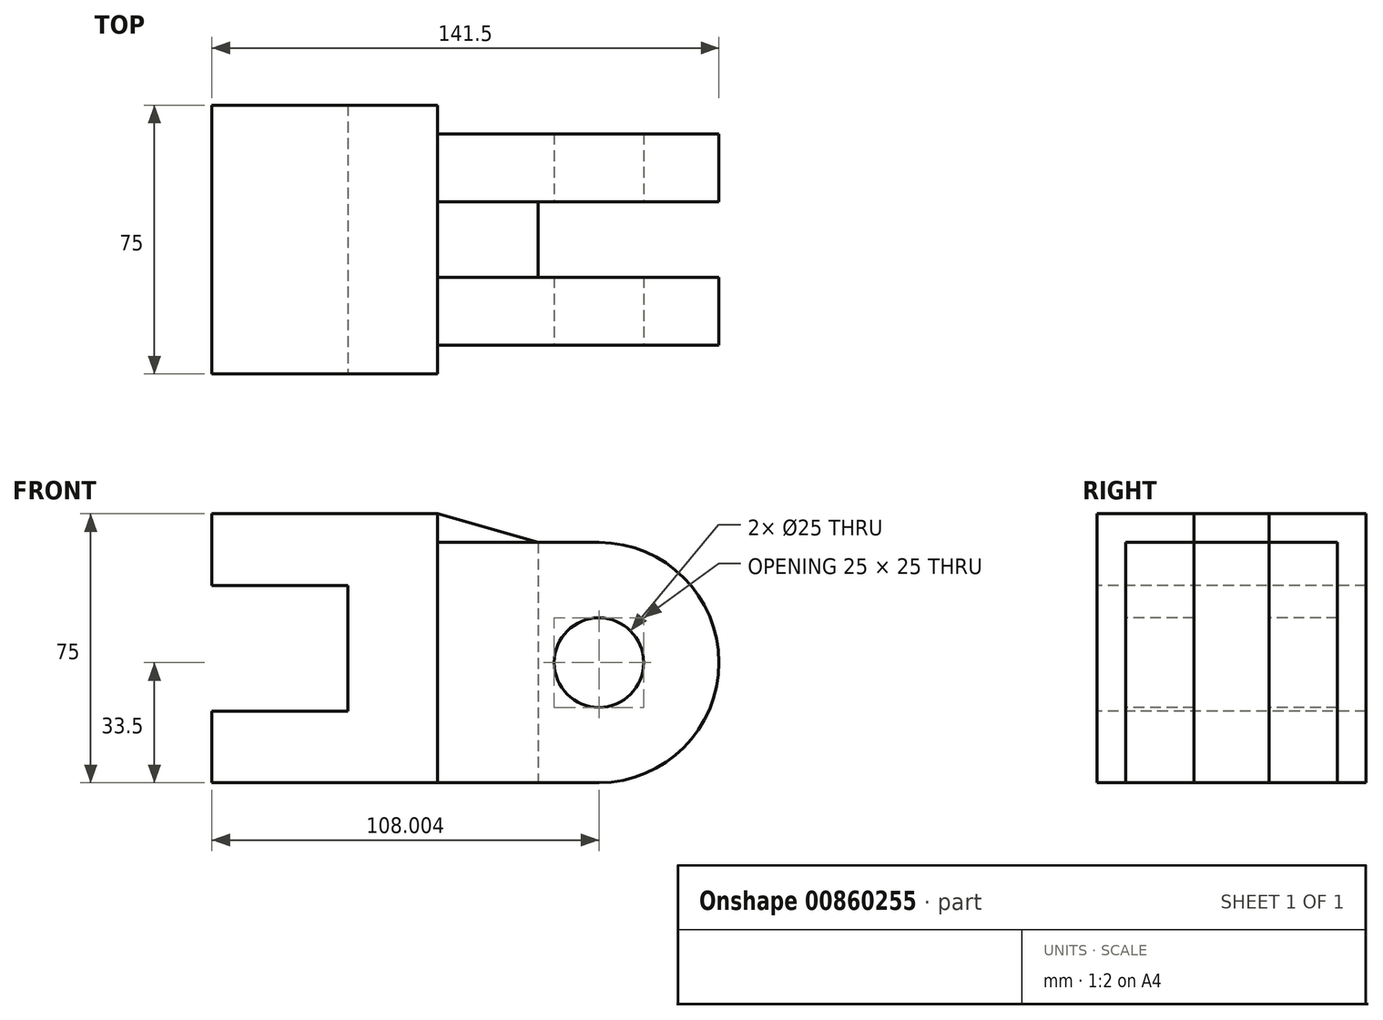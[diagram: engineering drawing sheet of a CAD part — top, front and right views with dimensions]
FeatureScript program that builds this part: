
annotation { "Feature Type Name" : "Feature", "Feature Type Description" : "" }
export const myFeature = defineFeature(function(context is Context, id is Id, definition is map)
    precondition{}
    {
        {
            var Q0;
            Q0=qCreatedBy(makeId("Top.planeOp"),FACE);
            var sketch = newSketch(context, id + "F0", { "sketchPlane" : qUnion([Q0])});
            skLineSegment(sketch, "E0.bottom", {"start": v(-50.72, 36.49) * mm, "end": v(12.28, 36.49) * mm});
            skLineSegment(sketch, "E0.top", {"start": v(-50.72, -38.51) * mm, "end": v(12.28, -38.51) * mm});
            skLineSegment(sketch, "E0.left", {"start": v(-50.72, 36.49) * mm, "end": v(-50.72, -38.51) * mm});
            skLineSegment(sketch, "E0.right", {"start": v(12.28, 36.49) * mm, "end": v(12.28, -38.51) * mm});
            skSolve(sketch);
        }
        {
            var Q0;
            Q0 = qSketchRegion(id + "F0", true);
            extrude(context, id + "F1", {"entities" : qUnion([Q0]), "depth" : 75 * mm, "offsetDistance" : 25 * mm});
        }
        {
            var Q0;
            Q0=makeQuery(id+"F1.opExtrude","SWEPT_FACE",FACE,{"disambiguationData":[OSD([sQuery(id+"F0.wireOp",EDGE,"E0.top")])]});
            var sketch = newSketch(context, id + "F2", { "sketchPlane" : qUnion([Q0])});
            skLineSegment(sketch, "E1", {"start": v(-50.72, 0) * mm, "end": v(-50.72, 20) * mm});
            skLineSegment(sketch, "E2", {"start": v(-50.72, 20) * mm, "end": v(-12.72, 20) * mm});
            skLineSegment(sketch, "E3", {"start": v(-12.72, 20) * mm, "end": v(-12.72, 55) * mm});
            skLineSegment(sketch, "E4", {"start": v(-12.72, 55) * mm, "end": v(-50.72, 55) * mm});
            skLineSegment(sketch, "E5", {"start": v(-50.72, 55) * mm, "end": v(-50.72, 75) * mm});
            skSolve(sketch);
        }
        {
            var Q0;
            {var subQ0=sQuery(id+"F2.wireOp",EDGE,"E2");Q0=makeQuery(id+"F2.imprint","IMPRINT",FACE,{"disambiguationData":[TD([[makeQuery(id+"F2.imprint","IMPRINT",EDGE,{"derivedFrom":subQ0}),1.0]])]});}
            extrude(context, id + "F3", {"entities" : qUnion([Q0]), "operationType" : NewBodyOperationType.REMOVE, "oppositeDirection" : true, "depth" : 75 * mm, "offsetDistance" : 25 * mm});
        }
        {
            var Q0;
            Q0=makeQuery(id+"F1.opExtrude","SWEPT_FACE",FACE,{"disambiguationData":[OSD([sQuery(id+"F0.wireOp",EDGE,"E0.right")])]});
            var sketch = newSketch(context, id + "F4", { "sketchPlane" : qUnion([Q0])});
            skLineSegment(sketch, "E6", {"start": v(-30.51, 67) * mm, "end": v(-30.51, 0) * mm});
            skLineSegment(sketch, "E7", {"start": v(-30.51, 0) * mm, "end": v(-11.51, 0) * mm});
            skLineSegment(sketch, "E8", {"start": v(-11.51, 0) * mm, "end": v(9.49, 0) * mm});
            skLineSegment(sketch, "E9", {"start": v(9.49, 0) * mm, "end": v(28.49, 0) * mm});
            skLineSegment(sketch, "E10", {"start": v(28.49, 0) * mm, "end": v(28.49, 67) * mm});
            skLineSegment(sketch, "E11", {"start": v(28.49, 67) * mm, "end": v(9.49, 67) * mm});
            skLineSegment(sketch, "E12", {"start": v(9.49, 67) * mm, "end": v(9.49, 0) * mm});
            skLineSegment(sketch, "E13", {"start": v(-30.51, 67) * mm, "end": v(-11.51, 67) * mm});
            skLineSegment(sketch, "E14", {"start": v(-11.51, 67) * mm, "end": v(-11.51, 0) * mm});
            skLineSegment(sketch, "E15", {"start": v(-11.51, 67) * mm, "end": v(-11.51, 75) * mm});
            skLineSegment(sketch, "E16", {"start": v(-11.51, 75) * mm, "end": v(9.49, 75) * mm});
            skLineSegment(sketch, "E17", {"start": v(9.49, 75) * mm, "end": v(9.49, 67) * mm});
            skSolve(sketch);
        }
        {
            var Q0;
            Q0=makeQuery(id+"F4.imprint","IMPRINT",FACE,{"disambiguationData":[TD([[makeQuery(id+"F4.imprint","IMPRINT",EDGE,{"derivedFrom":sQuery(id+"F4.wireOp",EDGE,"E6")}),1.0]])]});
            var Q1;
            Q1=makeQuery(id+"F4.imprint","IMPRINT",FACE,{"disambiguationData":[TD([[makeQuery(id+"F4.imprint","IMPRINT",EDGE,{"derivedFrom":sQuery(id+"F4.wireOp",EDGE,"E9")}),-1.0]])]});
            extrude(context, id + "F5", {"entities" : qUnion([Q0, Q1]), "operationType" : NewBodyOperationType.ADD, "depth" : 45 * mm, "offsetDistance" : 25 * mm});
        }
        {
            var Q0;
            Q0=makeQuery(id+"F1.opExtrude","SWEPT_FACE",FACE,{"disambiguationData":[OSD([sQuery(id+"F0.wireOp",EDGE,"E0.right")])]});
            var sketch = newSketch(context, id + "F6", { "sketchPlane" : qUnion([Q0])});
            skLineSegment(sketch, "E18", {"start": v(-11.51, 67) * mm, "end": v(-11.51, 75) * mm});
            skLineSegment(sketch, "E19", {"start": v(-11.51, 75) * mm, "end": v(9.49, 75) * mm});
            skLineSegment(sketch, "E20", {"start": v(9.49, 75) * mm, "end": v(9.49, 67) * mm});
            skLineSegment(sketch, "E21", {"start": v(9.49, 67) * mm, "end": v(9.49, 0) * mm});
            skLineSegment(sketch, "E22", {"start": v(9.49, 0) * mm, "end": v(-11.51, 0) * mm});
            skLineSegment(sketch, "E23", {"start": v(-11.51, 0) * mm, "end": v(-11.51, 67) * mm});
            skSolve(sketch);
        }
        {
            var Q0;
            Q0=makeQuery(id+"F6.imprint","IMPRINT",FACE,{"disambiguationData":[TD([[makeQuery(id+"F6.imprint","IMPRINT",EDGE,{"derivedFrom":sQuery(id+"F6.wireOp",EDGE,"E18")}),-1.0]])]});
            extrude(context, id + "F7", {"entities" : qUnion([Q0]), "operationType" : NewBodyOperationType.ADD, "depth" : 28 * mm, "offsetDistance" : 25 * mm});
        }
        {
            var Q0;
            Q0=makeQuery(id+"F7.opExtrude","SWEPT_FACE",FACE,{"disambiguationData":[OSD([sQuery(id+"F6.wireOp",EDGE,"E18"),sQuery(id+"F6.wireOp",EDGE,"E23")])]});
            var sketch = newSketch(context, id + "F8", { "sketchPlane" : qUnion([Q0])});
            skLineSegment(sketch, "E24", {"start": v(12.28, 75) * mm, "end": v(40.28, 67) * mm});
            skSolve(sketch);
        }
        {
            var Q0;
            Q0=makeQuery(id+"F8.imprint","IMPRINT",FACE,{"disambiguationData":[TD([[makeQuery(id+"F8.imprint","IMPRINT",EDGE,{"derivedFrom":sQuery(id+"F8.wireOp",EDGE,"E24")}),1.0]])]});
            extrude(context, id + "F9", {"entities" : qUnion([Q0]), "operationType" : NewBodyOperationType.REMOVE, "oppositeDirection" : true, "depth" : 25 * mm, "offsetDistance" : 25 * mm});
        }
        {
            var Q0;
            Q0=makeQuery(id+"F5.opExtrude","SWEPT_FACE",FACE,{"disambiguationData":[OSD([sQuery(id+"F4.wireOp",EDGE,"E6")])]});
            var sketch = newSketch(context, id + "F10", { "sketchPlane" : qUnion([Q0])});
            skArc(sketch, "E25", {"start": v(57.28, 0) * mm, "mid": v(90.78, 33.5) * mm, "end": v(57.28, 67) * mm});
            skSolve(sketch);
        }
        {
            var Q0;
            Q0=makeQuery(id+"F10.imprint","IMPRINT",FACE,{"disambiguationData":[TD([[makeQuery(id+"F10.imprint","IMPRINT",EDGE,{"derivedFrom":sQuery(id+"F10.wireOp",EDGE,"E25")}),1.0]])]});
            extrude(context, id + "F11", {"entities" : qUnion([Q0]), "operationType" : NewBodyOperationType.ADD, "oppositeDirection" : true, "depth" : 19 * mm, "offsetDistance" : 25 * mm});
        }
        {
            var Q0;
            Q0=makeQuery(id+"F5.opExtrude","SWEPT_FACE",FACE,{"disambiguationData":[OSD([sQuery(id+"F4.wireOp",EDGE,"E10")])]});
            var sketch = newSketch(context, id + "F12", { "sketchPlane" : qUnion([Q0])});
            skArc(sketch, "E26", {"start": v(-57.28, 67) * mm, "mid": v(-90.78, 33.5) * mm, "end": v(-57.28, 0) * mm});
            skSolve(sketch);
        }
        {
            var Q0;
            Q0=makeQuery(id+"F12.imprint","IMPRINT",FACE,{"disambiguationData":[TD([[makeQuery(id+"F12.imprint","IMPRINT",EDGE,{"derivedFrom":sQuery(id+"F12.wireOp",EDGE,"E26")}),1.0]])]});
            extrude(context, id + "F13", {"entities" : qUnion([Q0]), "operationType" : NewBodyOperationType.ADD, "oppositeDirection" : true, "depth" : 19 * mm, "offsetDistance" : 25 * mm});
        }
        {
            var Q0;
            {var subQ0=sQuery(id+"F4.wireOp",EDGE,"E6");Q0=makeQuery(id+"F11.boolean.opBoolean","MERGE",FACE,{"derivedFrom":[makeQuery(id+"F5.opExtrude","SWEPT_FACE",FACE,{"disambiguationData":[OSD([subQ0])]}),makeQuery(id+"F11.opExtrude","CAP_FACE",FACE,{"disambiguationData":[OSD([subQ0,sQuery(id+"F10.wireOp",EDGE,"E25")])],"isStart":true})]});}
            var sketch = newSketch(context, id + "F14", { "sketchPlane" : qUnion([Q0])});
            skLineSegment(sketch, "E27", {"start": v(12.28, 67) * mm, "end": v(57.28, 67) * mm});
            skLineSegment(sketch, "E28", {"start": v(57.28, 67) * mm, "end": v(57.28, 33.5) * mm});
            skCircle(sketch, "E29", {"center": v(57.28, 33.5) * mm, "radius": 12.5 * mm});
            skSolve(sketch);
        }
        {
            var Q0;
            Q0=makeQuery(id+"F14.imprint","IMPRINT",FACE,{"disambiguationData":[TD([[makeQuery(id+"F14.imprint","IMPRINT",EDGE,{"derivedFrom":sQuery(id+"F14.wireOp",EDGE,"E29")}),1.0]])]});
            extrude(context, id + "F15", {"entities" : qUnion([Q0]), "operationType" : NewBodyOperationType.REMOVE, "oppositeDirection" : true, "depth" : 100 * mm, "offsetDistance" : 25 * mm});
        }
    });
